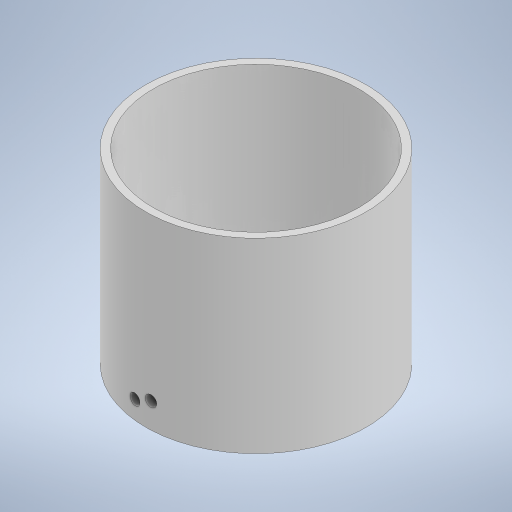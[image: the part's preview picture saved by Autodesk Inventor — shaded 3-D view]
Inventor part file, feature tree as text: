
AUTODESK INVENTOR PART (.ipt)
format: ipt  version: 2023 (Build 270158000, 158)  size: 218,624 bytes
history: native  units: in
note: dims shown in document units (in); Inventor stores cm internally (conversion verified against a paired STEP export)
features: extrude x2, sketch x2, shell x1, plane x1
ambient origin geometry x8: Origin, YZ Plane, XZ Plane, XY Plane, X Axis, Y Axis, Z Axis, Center Point
bodies: Solid1 (feature_tree)
feature tree (6):
  extrude  "Extrusion1"  Depth=0.0787in TaperAngle=0.0deg
  shell  "Shell1"  Thickness=0.0787in
  plane  "Work Plane1"
  extrude  "Extrusion2"  Depth=0.1181in
  sketch  "Sketch1"  dims[d0=2.3622in d1=2.0in d2=0.0in d3=0.0787in]
  sketch  "Sketch2"  dims[d4=0.1181in d5=0.1181in d6=0.1764in d7=0.0748in d8=0.1181in d9=0.1575in d10=0.0in]
